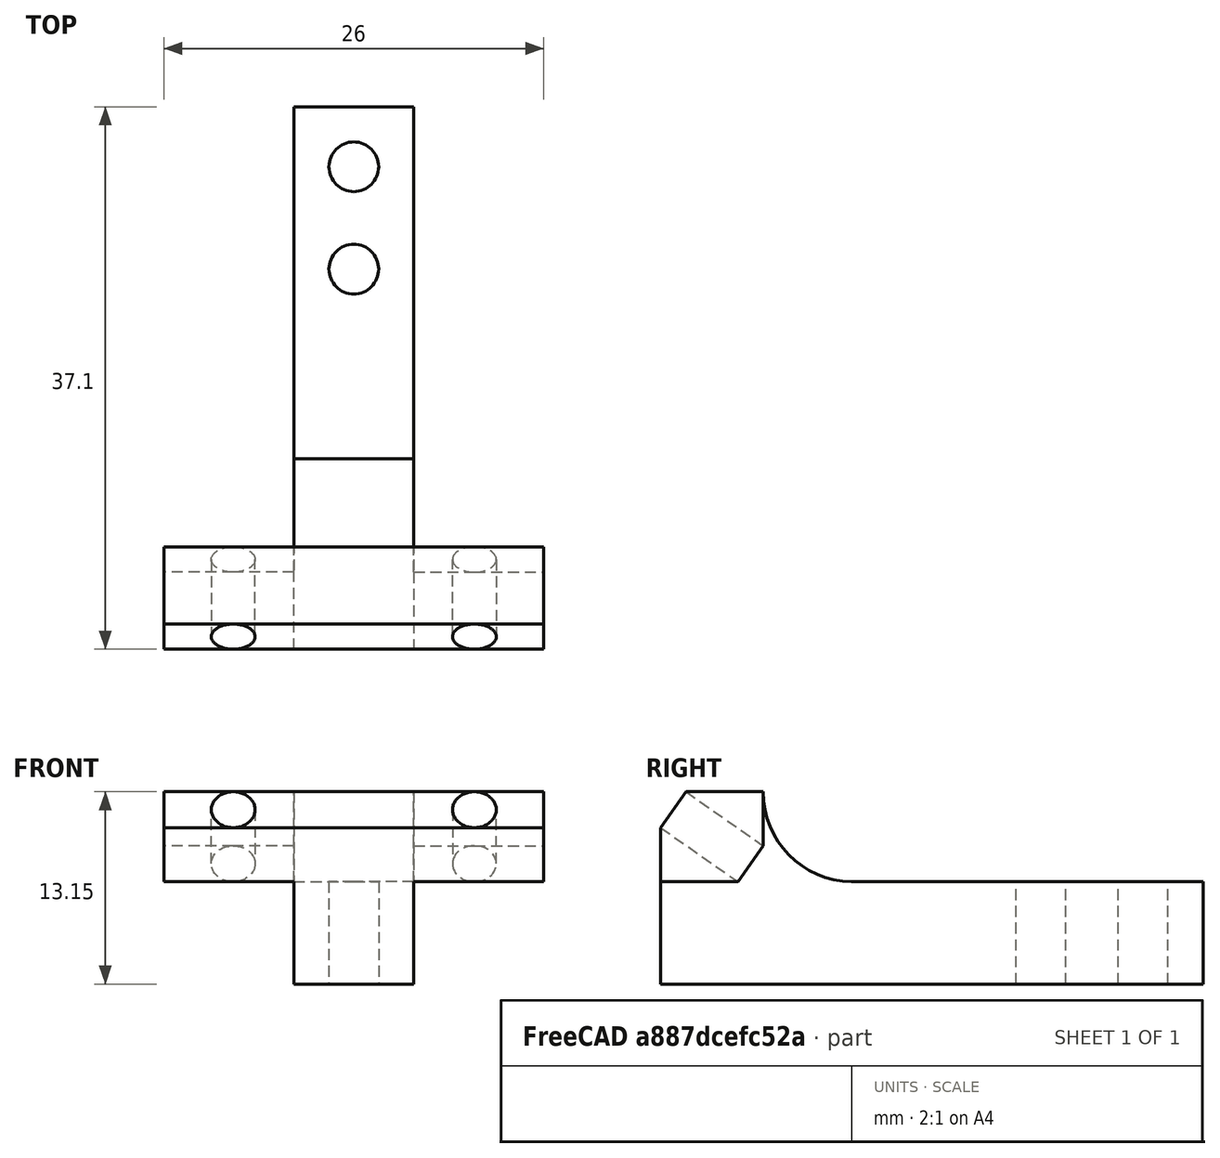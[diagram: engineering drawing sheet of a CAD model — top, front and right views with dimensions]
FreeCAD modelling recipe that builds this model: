
FCSTD DOCUMENT  (FreeCAD 0.19R24291 (Git))
Label: Иголки 55 2
License: All rights reserved
LicenseURL: http://en.wikipedia.org/wiki/All_rights_reserved
objects: Sketcher::SketchObject×4, PartDesign::Pad×3, Mesh::Feature×1, PartDesign::Pocket×1, PartDesign::Mirrored×1, PartDesign::Body×1
note: 14 computed .brp shape members not serialized (recipe doc carries the construction recipe); baked Part::Feature solids carry a one-line shape summary decoded from their .brp

FEATURE [Mesh::Feature] ____________55  label="Иголки55"
FEATURE [Sketcher::SketchObject] Sketch
  FullyConstrained = true
  MapMode = 5
  Support = -> [XY_Plane]
  sketch-geometry (8):
    g0: ArcOfCircle CenterX=0 CenterY=33 CenterZ=0 NormalX=0 NormalY=0 NormalZ=1 AngleXU=0 Radius=1.7 StartAngle=1.5708 EndAngle=4.71239
    g1: ArcOfCircle CenterX=0 CenterY=26 CenterZ=0 NormalX=0 NormalY=0 NormalZ=1 AngleXU=0 Radius=1.7 StartAngle=1.5708 EndAngle=4.71239
    g2: LineSegment StartX=1e-16 StartY=34.7 StartZ=0 EndX=0 EndY=37.1 EndZ=0
    g3: LineSegment StartX=0 StartY=37.1 StartZ=0 EndX=-4.1 EndY=37.1 EndZ=0
    g4: LineSegment StartX=-4.1 StartY=37.1 StartZ=0 EndX=-4.1 EndY=0 EndZ=0
    g5: LineSegment StartX=-4.1 StartY=0 StartZ=0 EndX=0 EndY=0 EndZ=0
    g6: LineSegment StartX=0 StartY=0 StartZ=0 EndX=-3e-16 EndY=24.3 EndZ=0
    g7: LineSegment StartX=1e-16 StartY=27.7 StartZ=0 EndX=-3e-16 EndY=31.3 EndZ=0
  constraints (26):
    c: PointOnObject(g0,g-2)
    c: PointOnObject(g0,g-2)
    c: PointOnObject(g0,g-2)
    c: PointOnObject(g1,g-2)
    c: PointOnObject(g1,g-2)
    c: PointOnObject(g1,g-2)
    c: Diameter(g1) = 3.4
    c: Equal(g1,g0)
    c: Distance(g1,g0) = 7
    c: Coincident(g2,g0)
    c: PointOnObject(g2,g-2)
    c: Distance(g2) = 2.4
    c: Coincident(g3,g2)
    c: Horizontal(g3)
    c: Distance(g1,g-1) = 26
    c: Distance(g3) = 4.1
    c: Coincident(g4,g3)
    c: PointOnObject(g4,g-1)
    c: Vertical(g4)
    c: Coincident(g5,g4)
    c: Coincident(g5,g-1)
    c: Coincident(g6,g5)
    c: Coincident(g6,g1)
    c: Coincident(g7,g1)
    c: Coincident(g7,g0)
    c: Distance(g4) = 37.1
FEATURE [PartDesign::Pad] Pad
  Direction = (1,1,1)
  Length = 7
  Length2 = 100
  Profile = -> Sketch
  Type = 0
FEATURE [Sketcher::SketchObject] Sketch001
  FullyConstrained = true
  MapMode = 5
  Placement = pos=(0,0,0) rot=(0.57735,0.57735,0.57735;2.0944rad)
  Support = -> [YZ_Plane]
  sketch-geometry (11):
    g0: LineSegment StartX=0 StartY=6.999 StartZ=0 EndX=5.27927 EndY=6.999 EndZ=0
    g1: LineSegment StartX=5.27927 StartY=6.999 StartZ=0 EndX=7 EndY=9.45646 EndZ=0
    g2: LineSegment StartX=7 StartY=9.45646 StartZ=0 EndX=7 EndY=13.153 EndZ=0
    g3: LineSegment StartX=7 StartY=13.153 StartZ=0 EndX=1.72073 EndY=13.153 EndZ=0
    g4: LineSegment StartX=1.72073 StartY=13.153 StartZ=0 EndX=0 EndY=10.6956 EndZ=0
    g5: LineSegment StartX=0 StartY=10.6956 StartZ=0 EndX=0 EndY=6.999 EndZ=0
    g6: LineSegment StartX=0 StartY=6.999 StartZ=0 EndX=7 EndY=6.999 EndZ=0
    g7: LineSegment StartX=7 StartY=6.999 StartZ=0 EndX=7 EndY=13.153 EndZ=0
    g8: LineSegment StartX=0 StartY=6.999 StartZ=0 EndX=0 EndY=13.153 EndZ=0
    g9: LineSegment StartX=0 StartY=13.153 StartZ=0 EndX=7 EndY=13.153 EndZ=0
    g10: LineSegment StartX=0 StartY=10.6956 StartZ=0 EndX=5.27927 EndY=6.999 EndZ=0
  constraints (30):
    c: PointOnObject(g0,g-2)
    c: Horizontal(g0)
    c: Coincident(g0,g1)
    c: Coincident(g1,g2)
    c: Vertical(g2)
    c: Coincident(g2,g3)
    c: Horizontal(g3)
    c: Coincident(g3,g4)
    c: PointOnObject(g4,g-2)
    c: Coincident(g4,g5)
    c: Coincident(g5,g0)
    c: Distance(g-1,g0) = 6.999
    c: Equal(g0,g3)
    c: Equal(g2,g5)
    c: DistanceX(g2) = 7
    c: Coincident(g6,g0)
    c: Horizontal(g6)
    c: Coincident(g7,g6)
    c: Coincident(g7,g2)
    c: Vertical(g7)
    c: Coincident(g8,g0)
    c: PointOnObject(g8,g-2)
    c: Coincident(g9,g8)
    c: Coincident(g9,g2)
    c: Horizontal(g9)
    c: Distance(g1) = 3
    c: Angle(g1,g6) = 2.18166
    c: Coincident(g10,g4)
    c: Coincident(g10,g0)
    c: Perpendicular(g10,g1)
FEATURE [PartDesign::Pad] Pad001
  BaseFeature = -> Pad
  Direction = (1,1,1)
  Length = 13
  Length2 = 100
  Profile = -> Sketch001
  Reversed = true
  Type = 0
FEATURE [Sketcher::SketchObject] Sketch002
  FullyConstrained = true
  MapMode = 5
  Placement = pos=(0,0,0) rot=(0.57735,0.57735,0.57735;2.0944rad)
  Support = -> [YZ_Plane]
  expr: Constraints[26] = Sketch001.Constraints[26]
  expr: Constraints[25] = Sketch001.Constraints[25]
  expr: Constraints[14] = Sketch001.Constraints[14]
  expr: Constraints[11] = Sketch001.Constraints[11]
  sketch-geometry (13):
    g0: LineSegment StartX=0 StartY=6.999 StartZ=0 EndX=5.27927 EndY=6.999 EndZ=0
    g1: LineSegment StartX=5.27927 StartY=6.999 StartZ=0 EndX=7 EndY=9.45646 EndZ=0
    g2: LineSegment StartX=7 StartY=9.45646 StartZ=0 EndX=7 EndY=13.153 EndZ=0
    g3: LineSegment StartX=7 StartY=13.153 StartZ=0 EndX=1.72073 EndY=13.153 EndZ=0
    g4: LineSegment StartX=1.72073 StartY=13.153 StartZ=0 EndX=-2e-16 EndY=10.6956 EndZ=0
    g5: LineSegment StartX=0 StartY=10.6956 StartZ=0 EndX=0 EndY=6.999 EndZ=0
    g6: LineSegment StartX=0 StartY=6.999 StartZ=0 EndX=7 EndY=6.999 EndZ=0
    g7: LineSegment StartX=7 StartY=6.999 StartZ=0 EndX=7 EndY=13.153 EndZ=0
    g8: LineSegment StartX=0 StartY=6.999 StartZ=0 EndX=0 EndY=13.153 EndZ=0
    g9: LineSegment StartX=0 StartY=13.153 StartZ=0 EndX=7 EndY=13.153 EndZ=0
    g10: LineSegment StartX=0 StartY=10.6956 StartZ=0 EndX=5.27927 EndY=6.999 EndZ=0
    g11: ArcOfCircle CenterX=13.154 CenterY=13.153 CenterZ=0 NormalX=0 NormalY=0 NormalZ=1 AngleXU=0 Radius=6.15404 StartAngle=3.14159 EndAngle=4.71239
    g12: LineSegment StartX=5.27927 StartY=6.999 StartZ=0 EndX=13.1541 EndY=6.999 EndZ=0
  constraints (36):
    c: PointOnObject(g0,g-2)
    c: Horizontal(g0)
    c: Coincident(g0,g1)
    c: Coincident(g1,g2)
    c: Vertical(g2)
    c: Coincident(g2,g3)
    c: Horizontal(g3)
    c: Coincident(g3,g4)
    c: PointOnObject(g4,g-2)
    c: Coincident(g4,g5)
    c: Coincident(g5,g0)
    c: Distance(g-1,g0) = 6.999
    c: Equal(g0,g3)
    c: Equal(g2,g5)
    c: DistanceX(g2) = 7
    c: Coincident(g6,g0)
    c: Horizontal(g6)
    c: Coincident(g7,g6)
    c: Coincident(g7,g2)
    c: Vertical(g7)
    c: Coincident(g8,g0)
    c: PointOnObject(g8,g-2)
    c: Coincident(g9,g8)
    c: Coincident(g9,g2)
    c: Horizontal(g9)
    c: Distance(g1) = 3
    c: Angle(g1,g6) = 2.18166
    c: Coincident(g10,g4)
    c: Coincident(g10,g0)
    c: Perpendicular(g10,g1)
    c: Coincident(g11,g2)
    c: Tangent(g11,g2)
    c: Coincident(g12,g1)
    c: Coincident(g12,g11)
    c: Horizontal(g12)
    c: Tangent(g12,g11)
FEATURE [PartDesign::Pad] Pad002
  BaseFeature = -> Pad001
  Direction = (1,1,1)
  Length = 4.1
  Length2 = 100
  Profile = -> Sketch002
  Reversed = true
  Type = 0
FEATURE [Sketcher::SketchObject] Sketch003
  ExternalGeometry = -> [Pad002]
  FullyConstrained = true
  MapMode = 5
  Placement = pos=(1e-16,0.253989,-0.177845) rot=(0,0.887011,0.461749;3.14159rad)
  Support = -> [Pad002]
  sketch-geometry (1):
    g0: Circle CenterX=8.25 CenterY=10.2613 CenterZ=0 NormalX=0 NormalY=0 NormalZ=1 AngleXU=0 Radius=1.5
  constraints (3):
    c: Tangent(g0,g-4)
    c: Tangent(g0,g-3)
    c: Distance(g0,g-2) = 8.25
FEATURE [PartDesign::Pocket] Pocket
  BaseFeature = -> Pad002
  Length = 5
  Length2 = 100
  Profile = -> Sketch003
  Type = 1
FEATURE [PartDesign::Mirrored] Mirrored
  BaseFeature = -> Pocket
  MirrorPlane = -> Sketch [V_Axis]
  Originals = -> [Pad,Pad001,Pad002,Pocket]
FEATURE [PartDesign::Body] Body
  Group = -> [Sketch,Pad,Sketch001,Pad001,Sketch002,Pad002,Sketch003,Pocket,Mirrored]
  Origin = -> Origin
  Tip = -> Mirrored
